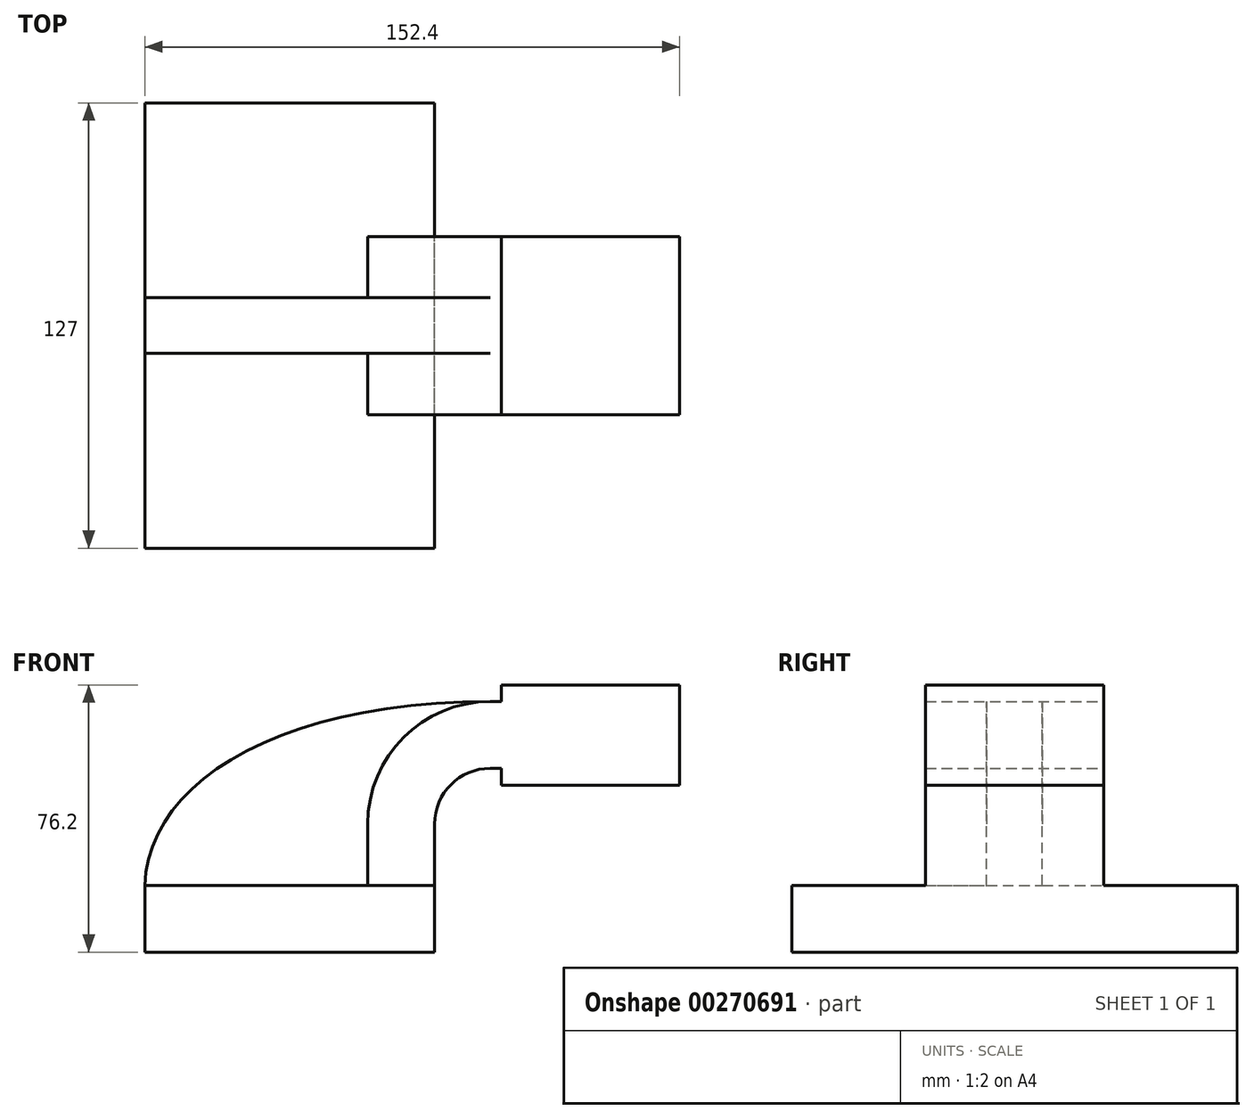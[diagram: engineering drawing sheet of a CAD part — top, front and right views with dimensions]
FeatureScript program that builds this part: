
annotation { "Feature Type Name" : "Feature", "Feature Type Description" : "" }
export const myFeature = defineFeature(function(context is Context, id is Id, definition is map)
    precondition{}
    {
        {
            var Q0;
            Q0=qCreatedBy(makeId("Front.planeOp"),FACE);
            var sketch = newSketch(context, id + "F0", { "sketchPlane" : qUnion([Q0])});
            skLineSegment(sketch, "E0.bottom", {"start": v(-41.27, -9.53) * mm, "end": v(41.28, -9.53) * mm});
            skLineSegment(sketch, "E0.top", {"start": v(-41.28, 9.52) * mm, "end": v(41.28, 9.52) * mm});
            skLineSegment(sketch, "E0.left", {"start": v(-41.28, -9.53) * mm, "end": v(-41.28, 9.52) * mm});
            skLineSegment(sketch, "E0.right", {"start": v(41.28, -9.53) * mm, "end": v(41.28, 9.52) * mm});
            skPoint(sketch, "E0.middle", {"position": v(0, 0) * mm});
            skLineSegment(sketch, "E1.bottom", {"start": v(60.32, 38.1) * mm, "end": v(111.12, 38.1) * mm});
            skLineSegment(sketch, "E1.top", {"start": v(60.32, 66.67) * mm, "end": v(111.12, 66.67) * mm});
            skLineSegment(sketch, "E1.left", {"start": v(60.32, 38.1) * mm, "end": v(60.32, 66.67) * mm});
            skLineSegment(sketch, "E1.right", {"start": v(111.12, 38.1) * mm, "end": v(111.12, 66.67) * mm});
            skPoint(sketch, "E1.middle", {"position": v(85.72, 52.39) * mm});
            skLineSegment(sketch, "E2", {"start": v(41.27, 9.52) * mm, "end": v(41.27, 27) * mm});
            skArc(sketch, "E3", {"start": v(41.27, 27) * mm, "mid": v(45.92, 38.23) * mm, "end": v(57.15, 42.88) * mm});
            skLineSegment(sketch, "E4", {"start": v(57.15, 42.88) * mm, "end": v(85.73, 42.88) * mm});
            skLineSegment(sketch, "E5.0", {"start": v(57.15, 61.93) * mm, "end": v(85.73, 61.93) * mm});
            skArc(sketch, "E5.1", {"start": v(22.22, 27) * mm, "mid": v(32.45, 51.7) * mm, "end": v(57.15, 61.93) * mm});
            skLineSegment(sketch, "E5.2", {"start": v(22.22, 9.52) * mm, "end": v(22.22, 27) * mm});
            skLineSegment(sketch, "E6", {"start": v(85.73, 42.88) * mm, "end": v(85.73, 61.93) * mm});
            skFitSpline(sketch, "E7", {"points": [v(-41.28, 9.53) * mm, v(57.15, 61.93) * mm], "startDerivative": vector(2.5, 87.12) * mm, "endDerivative": vector(182.26, 0.14) * mm});
            skSolve(sketch);
        }
        {
            var Q0;
            Q0=makeQuery(id+"F0.imprint","IMPRINT",FACE,{"disambiguationData":[TD([[makeQuery(id+"F0.imprint","IMPRINT",EDGE,{"derivedFrom":sQuery(id+"F0.wireOp",EDGE,"E0.bottom")}),1.0]])]});
            extrude(context, id + "F1", {"entities" : qUnion([Q0]), "endBound" : BoundingType.SYMMETRIC, "depth" : 127 * mm});
        }
        {
            var Q0;
            {var subQ4=sQuery(id+"F0.wireOp",EDGE,"E1.bottom");Q0=makeQuery(id+"F0.imprint","IMPRINT",FACE,{"disambiguationData":[TD([[makeQuery(id+"F0.imprint","IMPRINT",EDGE,{"derivedFrom":subQ4}),1.0]])]});}
            var Q1;
            Q1=makeQuery(id+"F0.imprint","IMPRINT",FACE,{"disambiguationData":[TD([[makeQuery(id+"F0.imprint","IMPRINT",EDGE,{"derivedFrom":sQuery(id+"F0.wireOp",EDGE,"E0.bottom")}),1.0]])]});
            var Q2;
            {var subQ5=sQuery(id+"F0.wireOp",EDGE,"E6");Q2=makeQuery(id+"F0.imprint","IMPRINT",FACE,{"disambiguationData":[TD([[makeQuery(id+"F0.imprint","IMPRINT",EDGE,{"derivedFrom":subQ5}),1.0]])]});}
            var Q3;
            {var subQ1=sQuery(id+"F0.wireOp",EDGE,"E2");Q3=makeQuery(id+"F0.imprint","IMPRINT",FACE,{"disambiguationData":[TD([[makeQuery(id+"F0.imprint","IMPRINT",EDGE,{"derivedFrom":subQ1}),1.0]])]});}
            extrude(context, id + "F2", {"entities" : qUnion([Q0, Q1, Q2, Q3]), "operationType" : NewBodyOperationType.ADD, "endBound" : BoundingType.SYMMETRIC, "depth" : 50.8 * mm});
        }
        {
            var Q0;
            Q0 = qSketchRegion(id + "F0", true);
            extrude(context, id + "F3", {"entities" : qUnion([Q0]), "operationType" : NewBodyOperationType.ADD, "endBound" : BoundingType.SYMMETRIC, "depth" : 15.88 * mm});
        }
    });
